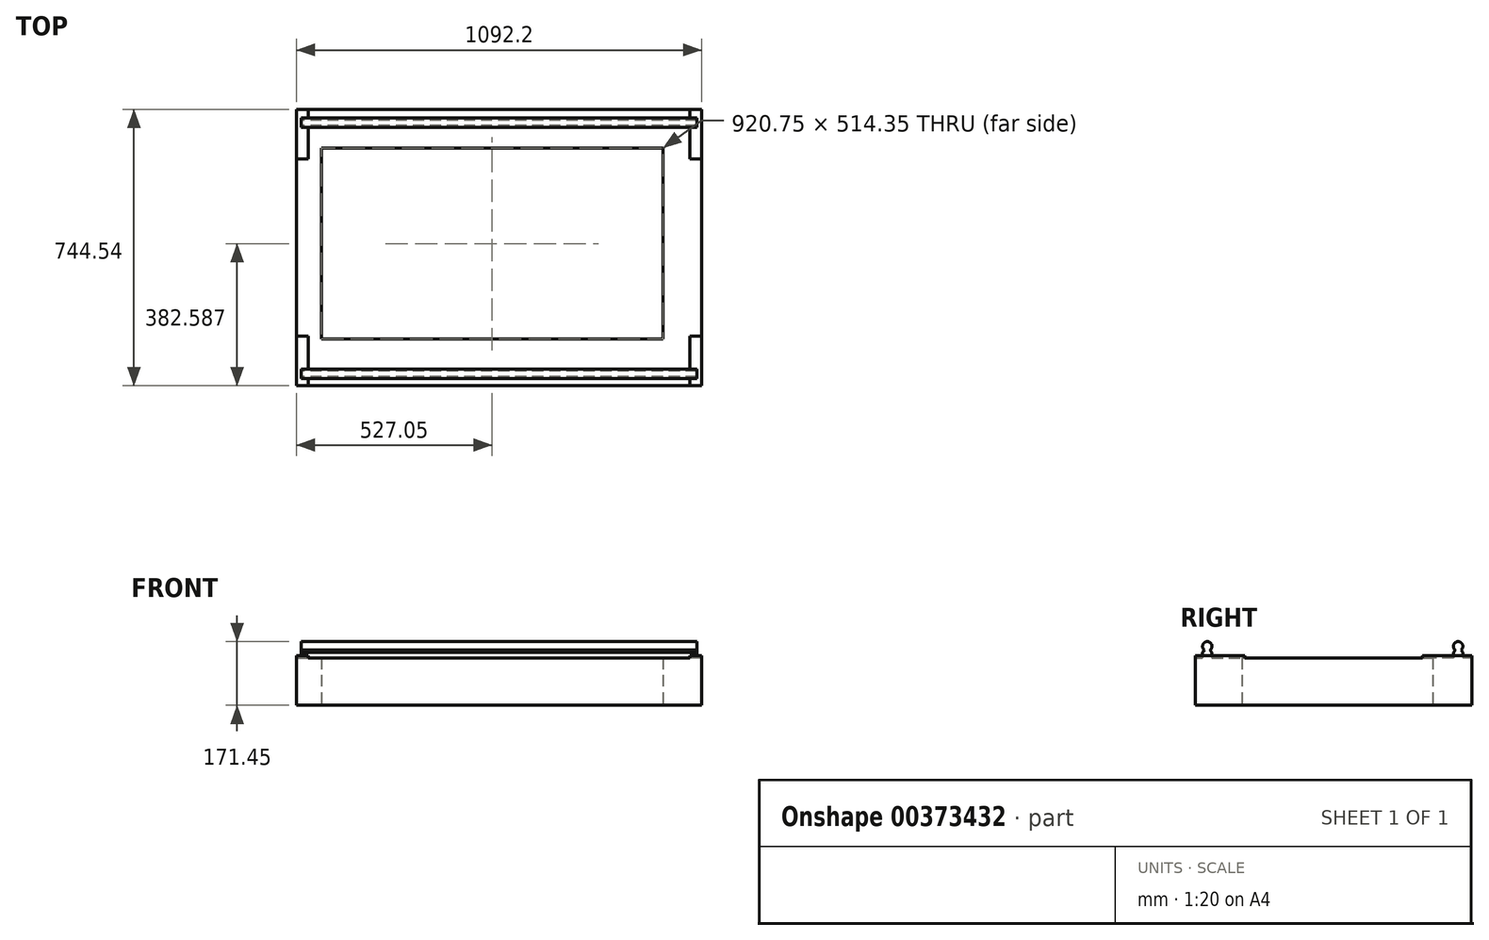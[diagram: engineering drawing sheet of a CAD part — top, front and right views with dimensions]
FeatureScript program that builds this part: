
annotation { "Feature Type Name" : "Feature", "Feature Type Description" : "" }
export const myFeature = defineFeature(function(context is Context, id is Id, definition is map)
    precondition{}
    {
        {
            var Q0;
            Q0=qCreatedBy(makeId("Top.planeOp"),FACE);
            var sketch = newSketch(context, id + "F0", { "sketchPlane" : qUnion([Q0])});
            skLineSegment(sketch, "E0.bottom", {"start": v(0, 0) * mm, "end": v(1092.2, 0) * mm});
            skLineSegment(sketch, "E0.top", {"start": v(0, 744.54) * mm, "end": v(1092.2, 744.54) * mm});
            skLineSegment(sketch, "E0.left", {"start": v(0, 0) * mm, "end": v(0, 744.54) * mm});
            skLineSegment(sketch, "E0.right", {"start": v(1092.2, 0) * mm, "end": v(1092.2, 744.54) * mm});
            skLineSegment(sketch, "E1.bottom", {"start": v(66.67, 125.41) * mm, "end": v(987.42, 125.41) * mm});
            skLineSegment(sketch, "E1.top", {"start": v(66.67, 639.76) * mm, "end": v(987.42, 639.76) * mm});
            skLineSegment(sketch, "E1.left", {"start": v(66.67, 125.41) * mm, "end": v(66.67, 639.76) * mm});
            skLineSegment(sketch, "E1.right", {"start": v(987.42, 125.41) * mm, "end": v(987.42, 639.76) * mm});
            skSolve(sketch);
        }
        {
            var Q0;
            Q0=makeQuery(id+"F0.imprint","IMPRINT",FACE,{"disambiguationData":[TD([[makeQuery(id+"F0.imprint","IMPRINT",EDGE,{"derivedFrom":sQuery(id+"F0.wireOp",EDGE,"E0.bottom")}),1.0]])]});
            extrude(context, id + "F1", {"entities" : qUnion([Q0]), "depth" : 127 * mm});
        }
        {
            var Q0;
            Q0=makeQuery(id+"F1.opExtrude","CAP_FACE",FACE,{"disambiguationData":[OSD([sQuery(id+"F0.wireOp",EDGE,"E0.bottom"),sQuery(id+"F0.wireOp",EDGE,"E0.top"),sQuery(id+"F0.wireOp",EDGE,"E0.left"),sQuery(id+"F0.wireOp",EDGE,"E0.right")])],"isStart":false});
            var sketch = newSketch(context, id + "F2", { "sketchPlane" : qUnion([Q0])});
            skLineSegment(sketch, "E2.bottom", {"start": v(12.7, 44.45) * mm, "end": v(1079.5, 44.45) * mm});
            skLineSegment(sketch, "E2.top", {"start": v(12.7, 19.05) * mm, "end": v(1079.5, 19.05) * mm});
            skLineSegment(sketch, "E2.left", {"start": v(12.7, 44.45) * mm, "end": v(12.7, 19.05) * mm});
            skLineSegment(sketch, "E2.right", {"start": v(1079.5, 44.45) * mm, "end": v(1079.5, 19.05) * mm});
            skLineSegment(sketch, "E3.bottom", {"start": v(12.7, 720.72) * mm, "end": v(1079.5, 720.72) * mm});
            skLineSegment(sketch, "E3.top", {"start": v(12.7, 695.33) * mm, "end": v(1079.5, 695.33) * mm});
            skLineSegment(sketch, "E3.left", {"start": v(12.7, 720.72) * mm, "end": v(12.7, 695.33) * mm});
            skLineSegment(sketch, "E3.right", {"start": v(1079.5, 720.72) * mm, "end": v(1079.5, 695.33) * mm});
            skSolve(sketch);
        }
        {
            var Q0;
            Q0=makeQuery(id+"F2.imprint","IMPRINT",FACE,{"disambiguationData":[TD([[makeQuery(id+"F2.imprint","IMPRINT",EDGE,{"derivedFrom":sQuery(id+"F2.wireOp",EDGE,"E2.bottom")}),-1.0]])]});
            var Q1;
            Q1=makeQuery(id+"F2.imprint","IMPRINT",FACE,{"disambiguationData":[TD([[makeQuery(id+"F2.imprint","IMPRINT",EDGE,{"derivedFrom":sQuery(id+"F2.wireOp",EDGE,"E3.bottom")}),-1.0]])]});
            extrude(context, id + "F3", {"entities" : qUnion([Q0, Q1]), "operationType" : NewBodyOperationType.ADD, "depth" : 25.4 * mm});
        }
        {
            var Q0;
            Q0=makeQuery(id+"F3.opExtrude","CAP_EDGE",EDGE,{"disambiguationData":[OSD([sQuery(id+"F2.wireOp",EDGE,"E2.top")])],"isStart":false});
            var Q1;
            Q1=makeQuery(id+"F3.opExtrude","CAP_EDGE",EDGE,{"disambiguationData":[OSD([sQuery(id+"F2.wireOp",EDGE,"E2.bottom")])],"isStart":false});
            var Q2;
            Q2=makeQuery(id+"F3.opExtrude","CAP_EDGE",EDGE,{"disambiguationData":[OSD([sQuery(id+"F2.wireOp",EDGE,"E3.bottom")])],"isStart":false});
            var Q3;
            Q3=makeQuery(id+"F3.opExtrude","CAP_EDGE",EDGE,{"disambiguationData":[OSD([sQuery(id+"F2.wireOp",EDGE,"E3.top")])],"isStart":false});
            chamfer(context, id + "F4", {"entities" : qUnion([Q0, Q1, Q2, Q3]), "width" : 9.52 * mm, "tangentPropagation" : true});
        }
        {
            var Q0;
            Q0=makeQuery(id+"F3.opExtrude","SWEPT_FACE",FACE,{"disambiguationData":[OSD([sQuery(id+"F2.wireOp",EDGE,"E2.left")])]});
            var sketch = newSketch(context, id + "F5", { "sketchPlane" : qUnion([Q0])});
            skCircle(sketch, "E4", {"center": v(-31.75, 158.75) * mm, "radius": 12.7 * mm});
            skCircle(sketch, "E5", {"center": v(-708.02, 158.75) * mm, "radius": 12.7 * mm});
            skSolve(sketch);
        }
        {
            var Q0;
            Q0=makeQuery(id+"F5.imprint","IMPRINT",FACE,{"disambiguationData":[TD([[makeQuery(id+"F5.imprint","IMPRINT",EDGE,{"derivedFrom":sQuery(id+"F5.wireOp",EDGE,"E5")}),1.0]])]});
            var Q1;
            {var subQ1=sQuery(id+"F2.wireOp",EDGE,"E2.left");var subQ7=makeQuery(id+"F3.opExtrude","CAP_EDGE",EDGE,{"disambiguationData":[OSD([subQ1])],"isStart":false});Q1=makeQuery(id+"F5.imprint","IMPRINT",FACE,{"disambiguationData":[TD([[makeQuery(id+"F5.imprint","IMPRINT",EDGE,{"derivedFrom":subQ7}),1.0]])]});}
            var Q2;
            {var subQ1=sQuery(id+"F2.wireOp",EDGE,"E2.left");var subQ7=makeQuery(id+"F3.opExtrude","CAP_EDGE",EDGE,{"disambiguationData":[OSD([subQ1])],"isStart":false});Q2=makeQuery(id+"F5.imprint","IMPRINT",FACE,{"disambiguationData":[TD([[makeQuery(id+"F5.imprint","IMPRINT",EDGE,{"derivedFrom":subQ7}),-1.0]])]});}
            extrude(context, id + "F6", {"entities" : qUnion([Q0, Q1, Q2]), "operationType" : NewBodyOperationType.ADD, "oppositeDirection" : true, "depth" : 1066.8 * mm});
        }
        {
            var Q0;
            Q0=makeQuery(id+"F1.opExtrude","CAP_FACE",FACE,{"disambiguationData":[OSD([sQuery(id+"F0.wireOp",EDGE,"E0.bottom"),sQuery(id+"F0.wireOp",EDGE,"E0.top"),sQuery(id+"F0.wireOp",EDGE,"E0.left"),sQuery(id+"F0.wireOp",EDGE,"E0.right")])],"isStart":false});
            var sketch = newSketch(context, id + "F7", { "sketchPlane" : qUnion([Q0])});
            skLineSegment(sketch, "E6.bottom", {"start": v(1092.2, 0) * mm, "end": v(1060.45, 0) * mm});
            skLineSegment(sketch, "E6.top", {"start": v(1092.2, 133.35) * mm, "end": v(1060.45, 133.35) * mm});
            skLineSegment(sketch, "E6.left", {"start": v(1092.2, 0) * mm, "end": v(1092.2, 133.35) * mm});
            skLineSegment(sketch, "E6.right", {"start": v(1060.45, 0) * mm, "end": v(1060.45, 133.35) * mm});
            skLineSegment(sketch, "E7.bottom", {"start": v(1092.2, 744.54) * mm, "end": v(1060.45, 744.54) * mm});
            skLineSegment(sketch, "E7.top", {"start": v(1092.2, 611.19) * mm, "end": v(1060.45, 611.19) * mm});
            skLineSegment(sketch, "E7.left", {"start": v(1092.2, 744.54) * mm, "end": v(1092.2, 611.19) * mm});
            skLineSegment(sketch, "E7.right", {"start": v(1060.45, 744.54) * mm, "end": v(1060.45, 611.19) * mm});
            skLineSegment(sketch, "E8.bottom", {"start": v(0, 744.54) * mm, "end": v(31.75, 744.54) * mm});
            skLineSegment(sketch, "E8.top", {"start": v(0, 611.19) * mm, "end": v(31.75, 611.19) * mm});
            skLineSegment(sketch, "E8.left", {"start": v(0, 744.54) * mm, "end": v(0, 611.19) * mm});
            skLineSegment(sketch, "E8.right", {"start": v(31.75, 744.54) * mm, "end": v(31.75, 611.19) * mm});
            skLineSegment(sketch, "E9.bottom", {"start": v(0, 0) * mm, "end": v(31.75, 0) * mm});
            skLineSegment(sketch, "E9.top", {"start": v(0, 133.35) * mm, "end": v(31.75, 133.35) * mm});
            skLineSegment(sketch, "E9.left", {"start": v(0, 0) * mm, "end": v(0, 133.35) * mm});
            skLineSegment(sketch, "E9.right", {"start": v(31.75, 0) * mm, "end": v(31.75, 133.35) * mm});
            skSolve(sketch);
        }
        {
            var Q0;
            {var subQ1=sQuery(id+"F7.wireOp",EDGE,"E9.bottom");Q0=makeQuery(id+"F7.imprint","IMPRINT",FACE,{"disambiguationData":[TD([[makeQuery(id+"F7.imprint","IMPRINT",EDGE,{"derivedFrom":subQ1}),1.0]])]});}
            var Q1;
            {var subQ1=sQuery(id+"F7.wireOp",EDGE,"E8.bottom");Q1=makeQuery(id+"F7.imprint","IMPRINT",FACE,{"disambiguationData":[TD([[makeQuery(id+"F7.imprint","IMPRINT",EDGE,{"derivedFrom":subQ1}),-1.0]])]});}
            var Q2;
            {var subQ1=sQuery(id+"F7.wireOp",EDGE,"E7.bottom");Q2=makeQuery(id+"F7.imprint","IMPRINT",FACE,{"disambiguationData":[TD([[makeQuery(id+"F7.imprint","IMPRINT",EDGE,{"derivedFrom":subQ1}),-1.0]])]});}
            var Q3;
            {var subQ1=sQuery(id+"F7.wireOp",EDGE,"E6.bottom");Q3=makeQuery(id+"F7.imprint","IMPRINT",FACE,{"disambiguationData":[TD([[makeQuery(id+"F7.imprint","IMPRINT",EDGE,{"derivedFrom":subQ1}),1.0]])]});}
            extrude(context, id + "F8", {"entities" : qUnion([Q0, Q1, Q2, Q3]), "operationType" : NewBodyOperationType.ADD, "depth" : 6.35 * mm});
        }
    });
